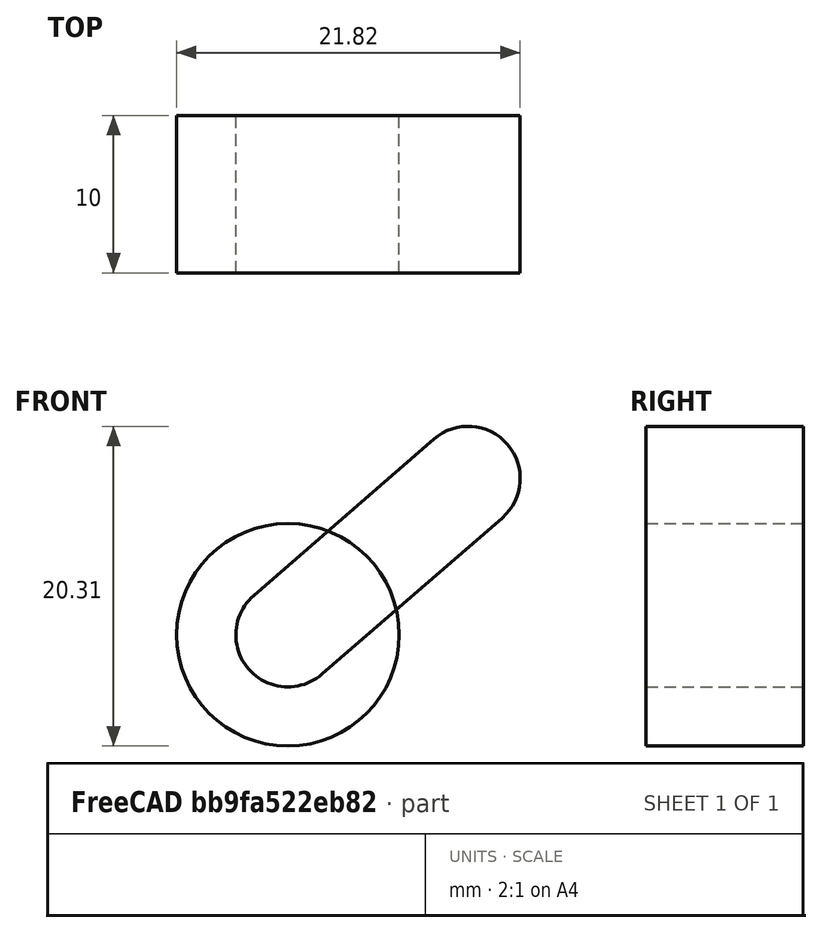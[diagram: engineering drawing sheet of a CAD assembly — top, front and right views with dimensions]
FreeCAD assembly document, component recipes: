
FREECAD ASSEMBLY — COMPONENT RECIPES ("TestInsert1-1")

This assembly document has 2 components, labeled P0..P1 below (a component is one placed body or linked part). 2 of them carry a construction recipe — the FreeCAD feature program that regenerates the part from scratch, quoted from this document or its linked companion documents; the rest are supplied as boundary geometry only. No exploded tour is included for this assembly.
COMPONENT P0 — recipe-attached ("Corps", modeled in this document).
Construction recipe (the document's own serialized feature program — sketch geometry with constraints, then the solid features built on it; lengths are millimeters unless a unit is written):

FEATURE [Sketcher::SketchObject] Sketch
  ArcFitTolerance = 1e-06
  AttachmentSupport = -> [Origin002]
  ExternalTypes = [0]
  FullyConstrained = false
  MakeInternals = false
  MapMode = 5
  Placement = pos=(0,0,0) rot=(1,0,0;1.5708rad)
  sketch-geometry (4):
    g0: ArcOfCircle CenterX=0 CenterY=0 CenterZ=0 NormalX=0 NormalY=0 NormalZ=1 AngleXU=0 Radius=3.30838 StartAngle=2.28574 EndAngle=5.42733
    g1: ArcOfCircle CenterX=11.4427 CenterY=9.93411 CenterZ=0 NormalX=0 NormalY=0 NormalZ=1 AngleXU=0 Radius=3.30838 StartAngle=5.42733 EndAngle=8.56893
    g2: LineSegment StartX=-2.1689 StartY=2.49826 StartZ=0 EndX=9.27378 EndY=12.4324 EndZ=0
    g3: LineSegment StartX=2.1689 StartY=-2.49826 StartZ=0 EndX=13.6116 EndY=7.43585 EndZ=0
  constraints (6):
    c: Tangent(g0,g2) = 1.5708
    c: Tangent(g0,g3) = -1.5708
    c: Tangent(g1,g2) = 1.5708
    c: Tangent(g1,g3) = -1.5708
    c: Equal(g0,g1)
    c: Coincident(g0,g-1)
FEATURE [PartDesign::Pad] Pad
  Direction = (0,-1,0)
  Length = 10
  Length2 = 10
  Profile = -> Sketch
  ReferenceAxis = -> Sketch [N_Axis]
  Refine = true
  SideType = 0
  Suppressed = false
  Type = 0
  Type2 = 0
FEATURE [PartDesign::Body] Body  label="Corps"
  AllowCompound = false
  Group = -> [Sketch,Pad]
  Origin = -> Origin002
  Tip = -> Pad
COMPONENT P1 — recipe-attached ("Corps001", modeled in this document).
Construction recipe (the document's own serialized feature program — sketch geometry with constraints, then the solid features built on it; lengths are millimeters unless a unit is written):

FEATURE [Sketcher::SketchObject] Sketch001
  ArcFitTolerance = 1e-06
  AttachmentSupport = -> [Origin004]
  ExternalTypes = [0]
  FullyConstrained = false
  MakeInternals = false
  MapMode = 5
  Placement = pos=(0,0,0) rot=(1,0,0;1.5708rad)
  sketch-geometry (1):
    g0: Circle CenterX=0 CenterY=0 CenterZ=0 NormalX=0 NormalY=0 NormalZ=1 AngleXU=0 Radius=7.06658
  constraints (1):
    c: Coincident(g0,g-1)
FEATURE [PartDesign::Pad] Pad001
  Direction = (0,-1,0)
  Length = 10
  Length2 = 10
  Profile = -> Sketch001
  ReferenceAxis = -> Sketch001 [N_Axis]
  Refine = true
  SideType = 0
  Suppressed = false
  Type = 0
  Type2 = 0
FEATURE [PartDesign::Body] Body001  label="Corps001"
  AllowCompound = false
  Group = -> [Sketch001,Pad001]
  Origin = -> Origin004
  Placement = pos=(-4.1e-15,3.6e-15,-4.7e-15) rot=(0,-1,0;4.71239rad)
  Tip = -> Pad001
PROVENANCE & LICENSES
A FreeCAD (.FCStd) document from a public repository crawl; recipes are the document's own serialized feature recipes (and, for linked parts, companion documents' recipes).
License: as declared in the source repository (recorded in the dataset sidecar).
